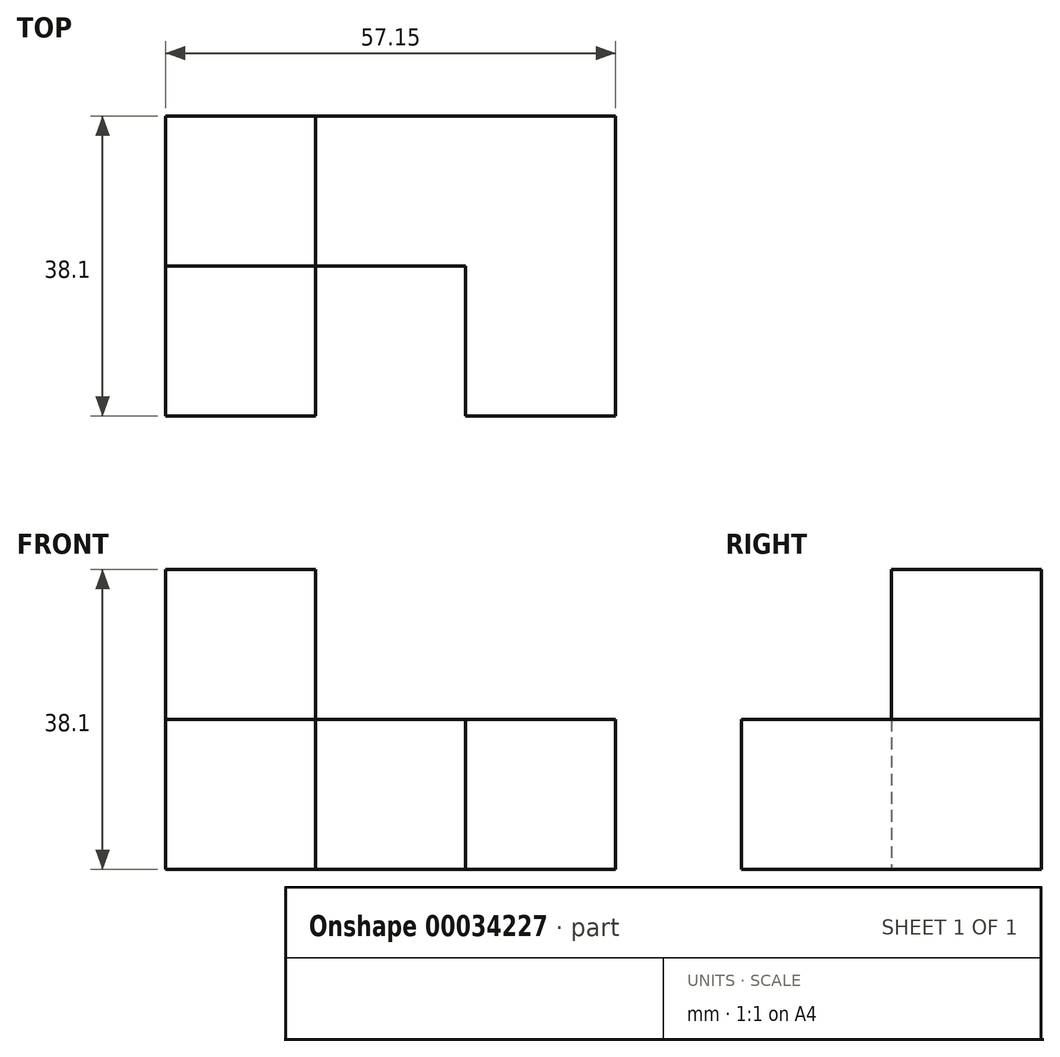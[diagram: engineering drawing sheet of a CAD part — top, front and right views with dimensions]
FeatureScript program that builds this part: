
annotation { "Feature Type Name" : "Feature", "Feature Type Description" : "" }
export const myFeature = defineFeature(function(context is Context, id is Id, definition is map)
    precondition{}
    {
        {
            var Q0;
            Q0=qCreatedBy(makeId("Top.planeOp"),FACE);
            var sketch = newSketch(context, id + "F0", { "sketchPlane" : qUnion([Q0])});
            skLineSegment(sketch, "E0.bottom", {"start": v(-28.58, 0) * mm, "end": v(28.58, 0) * mm});
            skLineSegment(sketch, "E0.top", {"start": v(-28.58, 0) * mm, "end": v(28.58, 0) * mm});
            skLineSegment(sketch, "E0.left", {"start": v(-28.58, 0) * mm, "end": v(-28.58, 0) * mm});
            skLineSegment(sketch, "E0.right", {"start": v(28.58, 0) * mm, "end": v(28.58, 0) * mm});
            skLineSegment(sketch, "E1.top", {"start": v(-28.58, -19.05) * mm, "end": v(28.58, -19.05) * mm});
            skLineSegment(sketch, "E1.left", {"start": v(-28.58, 0) * mm, "end": v(-28.58, -19.05) * mm});
            skLineSegment(sketch, "E1.right", {"start": v(28.58, 0) * mm, "end": v(28.58, -19.05) * mm});
            skLineSegment(sketch, "E2.bottom", {"start": v(-28.58, 0) * mm, "end": v(-9.53, 0) * mm});
            skLineSegment(sketch, "E2.top", {"start": v(-28.58, 19.05) * mm, "end": v(-9.53, 19.05) * mm});
            skLineSegment(sketch, "E2.left", {"start": v(-28.58, 0) * mm, "end": v(-28.58, 19.05) * mm});
            skLineSegment(sketch, "E2.right", {"start": v(-9.53, 0) * mm, "end": v(-9.53, 19.05) * mm});
            skLineSegment(sketch, "E3.bottom", {"start": v(28.58, 0) * mm, "end": v(9.53, 0) * mm});
            skLineSegment(sketch, "E3.top", {"start": v(28.58, 19.05) * mm, "end": v(9.53, 19.05) * mm});
            skLineSegment(sketch, "E3.left", {"start": v(28.58, 0) * mm, "end": v(28.58, 19.05) * mm});
            skLineSegment(sketch, "E3.right", {"start": v(9.53, 0) * mm, "end": v(9.53, 19.05) * mm});
            skSolve(sketch);
        }
        {
            var Q0;
            Q0 = qSketchRegion(id + "F0", true);
            extrude(context, id + "F1", {"entities" : qUnion([Q0]), "depth" : 19.05 * mm});
        }
        {
            var Q0;
            Q0=qCreatedBy(makeId("Top.planeOp"),FACE);
            var sketch = newSketch(context, id + "F2", { "sketchPlane" : qUnion([Q0])});
            skLineSegment(sketch, "E4.bottom", {"start": v(28.58, -19.05) * mm, "end": v(9.53, -19.05) * mm});
            skLineSegment(sketch, "E4.top", {"start": v(28.57, 0) * mm, "end": v(9.52, 0) * mm});
            skLineSegment(sketch, "E4.left", {"start": v(28.58, -19.05) * mm, "end": v(28.57, 0) * mm});
            skLineSegment(sketch, "E4.right", {"start": v(9.53, -19.05) * mm, "end": v(9.52, 0) * mm});
            skSolve(sketch);
        }
        {
            var Q0;
            Q0 = qSketchRegion(id + "F2", true);
            extrude(context, id + "F3", {"entities" : qUnion([Q0]), "operationType" : NewBodyOperationType.ADD, "depth" : 38.1 * mm});
        }
        {
            var Q0;
            Q0=makeQuery(id+"F3.boolean.opBoolean","MERGE",FACE,{"derivedFrom":[makeQuery(id+"F1.opExtrude","SWEPT_FACE",FACE,{"disambiguationData":[OSD([sQuery(id+"F0.wireOp",EDGE,"E1.top")])]}),makeQuery(id+"F3.opExtrude","SWEPT_FACE",FACE,{"disambiguationData":[OSD([sQuery(id+"F2.wireOp",EDGE,"E4.bottom")])]})]});
            var sketch = newSketch(context, id + "F4", { "sketchPlane" : qUnion([Q0])});
            skLineSegment(sketch, "E5", {"start": v(-28.58, 19.05) * mm, "end": v(-28.58, 0) * mm});
            skSolve(sketch);
        }
        {
            var Q0;
            Q0=makeQuery(id+"F1.opExtrude","SWEPT_BODY",BODY,{"disambiguationData":[OSD([sQuery(id+"F0.wireOp",EDGE,"E0.bottom"),sQuery(id+"F0.wireOp",EDGE,"E1.top"),sQuery(id+"F0.wireOp",EDGE,"E1.left"),sQuery(id+"F0.wireOp",EDGE,"E1.right"),sQuery(id+"F0.wireOp",EDGE,"E2.top"),sQuery(id+"F0.wireOp",EDGE,"E2.left"),sQuery(id+"F0.wireOp",EDGE,"E2.right"),sQuery(id+"F0.wireOp",EDGE,"E3.top"),sQuery(id+"F0.wireOp",EDGE,"E3.left"),sQuery(id+"F0.wireOp",EDGE,"E3.right")])]});
            var Q1;
            Q1=sQuery(id+"F4.wireOp",EDGE,"E5");
            var Q2;
            Q2=sQuery(id+"F4.wireOp",EDGE,"E5");
            transform(context, id + "F5", {"entities" : qUnion([Q0]), "transformType" : TransformType.ROTATION, "transformAxis" : qUnion([Q2]), "angle" : 180 * degree, "makeCopy" : false});
        }
    });
